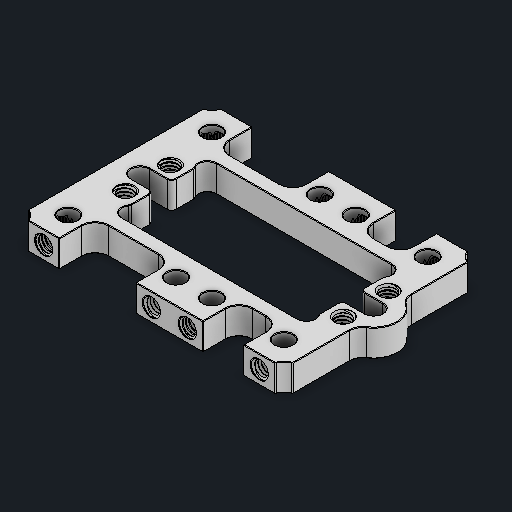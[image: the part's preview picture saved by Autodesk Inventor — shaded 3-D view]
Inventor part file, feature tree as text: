
AUTODESK INVENTOR PART (.ipt)
format: ipt  version: 2024 (Build 280153000, 153)  size: 4,546,048 bytes
history: native  units: in
note: dims shown in document units (in); Inventor stores cm internally (conversion verified against a paired STEP export)
features: chamfer x1
ambient origin geometry x8: Origin, YZ Plane, XZ Plane, XY Plane, X Axis, Y Axis, Z Axis, Center Point
bodies: Solid1 (feature_tree)
feature tree (1):
  chamfer  "Chamfer6"  [1 undecoded]
note: 1 required parameter value undecoded (feature->parameter linkage not recoverable at this tier; creation-order binding heuristic only, values carry confidence <= 0.55)
